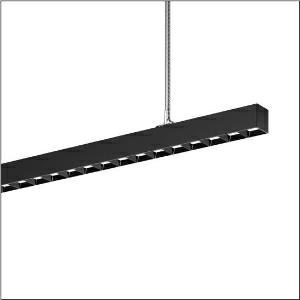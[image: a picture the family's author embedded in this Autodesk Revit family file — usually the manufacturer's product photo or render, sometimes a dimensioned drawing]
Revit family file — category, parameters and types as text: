
# Revit family: silica_r__21_51mx31tctdb_123f
name_source: partatom
category: Lighting Fixtures
units: mm (PartAtom-declared; Revit-internal decimal feet)

## family parameters
Cut with Voids When Loaded = No
Host = Face
Light Source = No
Part Type = Normal
Room Calculation Point = No
Round Connector Dimension = Use Diameter
Shared = No

## types (1)
- --- (1 x LED, 15550 lm, 133.9 W, 6500K)
    Apparent Load = 134 VA
    CIE Flux Codes = 85 99 100 60 100
    Color Rendering = 80
    Color Temperature = 6500K
    Default Elevation = 1800 mm
    Description = Silica® 21, office luminaire, primary light control with darklight reflector, of PMMA, black, CAT 2 (L<= 3000cd/m²), light emission: direct/indirect distribution, primary light characteristic: symmetric, installation type: suspended mounting, LED, rated luminous flux: 15.550lm, luminous efficacy: 111lm/W, light colour: 8tw, colour temperature: 2700..6500K, control gear: ECG DALI, with terminal, 3+2-pole, max. 2.5mm², mains connection: 220..240V, AC, 50/60Hz, rated input power: 140.6W, luminaire housing, of aluminium, jet black (RAL 9005), length: 3.004mm, width: 53mm, height: 53mm, protection rating (complete): IP20, insulation class (complete): insulation class I (protective earthing), certification: CE, permissible operating ambient temperature: 0..+35°C, standard: EN 50419, packaging unit: 1 piece
    Height = 53 mm
    Lamp = 1 x LED
    Lamp Light Flux = 15550 lm
    Lamp Power = 133.9 W
    Lamp count = 1
    Length = 3004 mm
    Luminous efficacy = 116 lm/W
    Manufacturer = Siteco
    ModVariant = No
    Model = 51MX31TCTDB
    Mounting Place = Ceiling
    Mounting Type = Pendant
    Number of Poles = 1
    OnlyDefault = Yes
    Power Factor = 1
    Product Name = Silica® 21
    Product group = office luminaire | ceiling pendant
    ProductGroupID = 902
    Protection Class = Protection class I
    Protection Degree = IP 20
    RLX_Detail_Level = 1
    RLX_Emergency_Light_Flux = 0 lm
    RLX_Emergency_Type = 0
    RLX_Emergency_Type_DB = No
    RlxData = <blob elided: 65581 chars, md5=08aed33e>
    Socket = socket
    Standby Power = 0 W
    System Light Flux = 15550 lm
    System Power = 134 W
    Type Comments = individual setting
    Type Image = l_1313617.jpg
    URL = http://relux.com
    VarID = @adj_089247
    Voltage = 0 V
    Weight = 0.00 kg
    Width = 53 mm

## geometry (parser evidence)
native form markers: Blend x4, Sweep x11
no freeform markers — native parametric forms only
